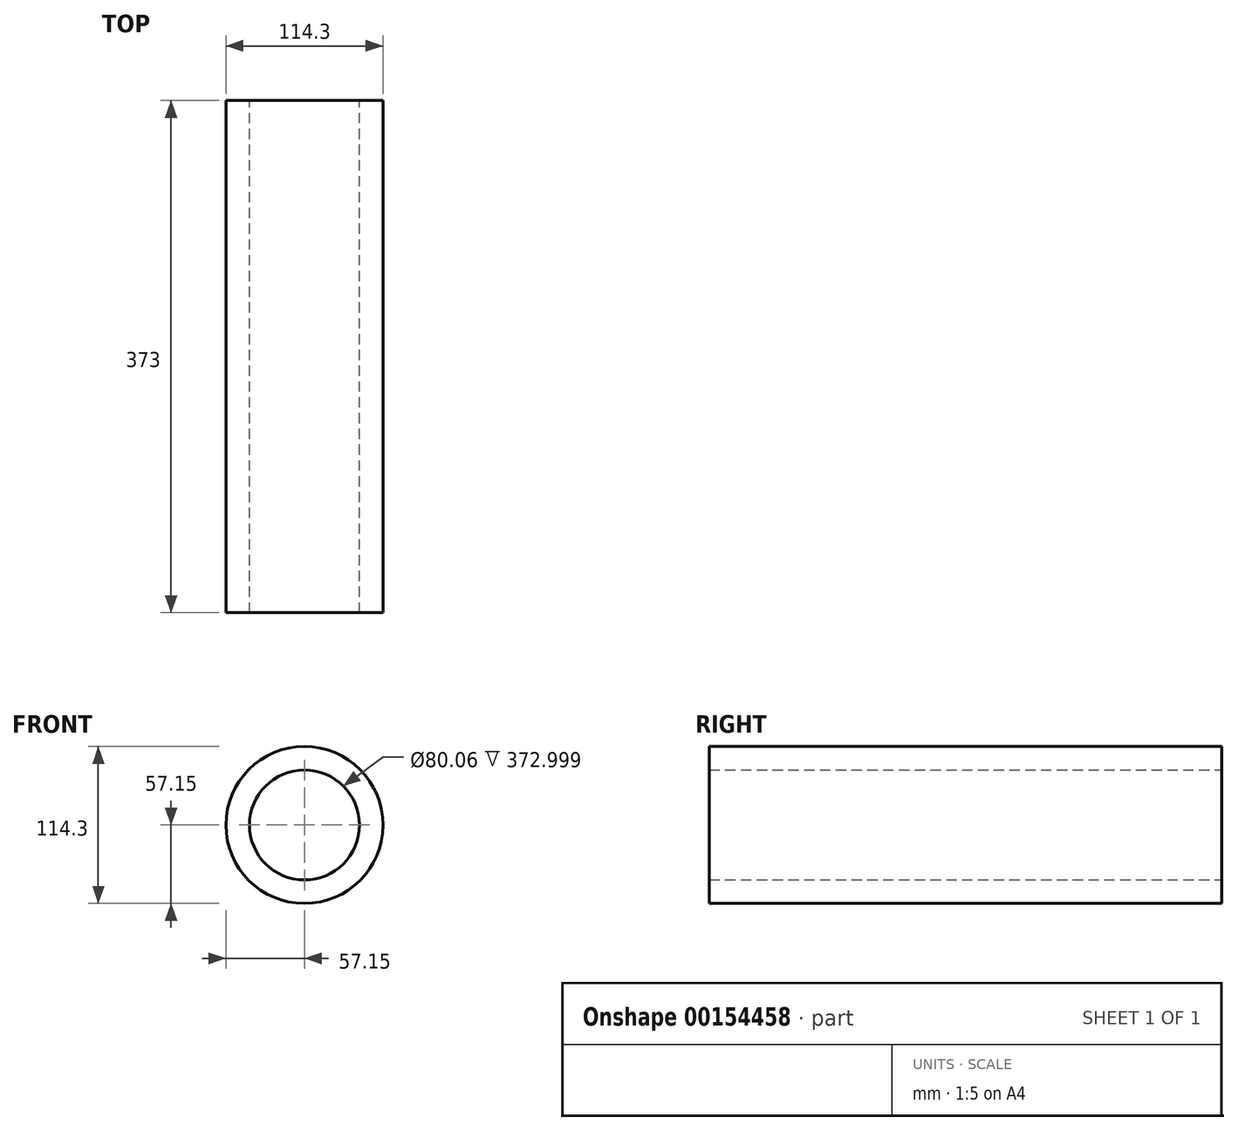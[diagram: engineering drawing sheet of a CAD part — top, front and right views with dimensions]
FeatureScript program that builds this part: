
annotation { "Feature Type Name" : "Feature", "Feature Type Description" : "" }
export const myFeature = defineFeature(function(context is Context, id is Id, definition is map)
    precondition{}
    {
        {
            var Q0;
            Q0=qCreatedBy(makeId("Front.planeOp"),FACE);
            var sketch = newSketch(context, id + "F0", { "sketchPlane" : qUnion([Q0])});
            skCircle(sketch, "E0", {"center": v(0, 0) * mm, "radius": 57.15 * mm});
            skCircle(sketch, "E1.0", {"center": v(0, 0) * mm, "radius": 40.03 * mm});
            skSolve(sketch);
        }
        {
            var Q0;
            Q0=makeQuery(id+"F0.imprint","IMPRINT",FACE,{"disambiguationData":[TD([[makeQuery(id+"F0.imprint","IMPRINT",EDGE,{"derivedFrom":sQuery(id+"F0.wireOp",EDGE,"E0")}),1.0]])]});
            extrude(context, id + "F1", {"entities" : qUnion([Q0]), "depth" : 373 * mm});
        }
    });
